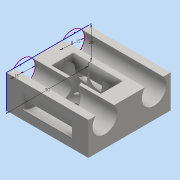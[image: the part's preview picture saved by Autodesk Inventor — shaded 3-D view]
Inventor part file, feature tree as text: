
AUTODESK INVENTOR PART (.ipt)
format: ipt  version: 2016 (Build 200138000, 138)  size: 208,384 bytes
history: native  units: mm
features: sketch x4, extrude x3, hole x1
ambient origin geometry x8: Origin, YZ Plane, XZ Plane, XY Plane, X Axis, Y Axis, Z Axis, Center Point
bodies: Body1 (feature_tree)
feature tree (8):
  sketch  "Sketch2"  dims[d22=50.0mm d23=20.0mm]
  extrude  "Extrusion2"  Depth=20.0mm
  extrude  "Extrusion3"  Depth=15.0mm
  extrude  "Extrusion4"  Depth=10.0mm
  hole  "Hole3"  [1 undecoded]
  sketch  "Sketch3"  dims[d24=15.0mm d25=15.0mm]
  sketch  "Sketch4"  dims[d26=10.0mm d27=0.0mm]
  sketch  "Sketch6"  dims[d28=50.0mm d29=20.0mm d30=15.0mm d31=15.0mm d32=30.0mm d33=0.0mm d34=50.0mm d35=20.0mm d36=15.0mm d37=15.0mm d38=10.0mm d39=0.0mm d47=3.0mm d48=25.0mm d49=3.0mm d50=4.5mm d51=10.0mm d52=3.0mm d53=4.5mm d54=3.2mm d55=6.0mm d56=8.0mm d57=15.0mm d58=90.0deg d59=8.0mm d60=20.594885mm d40=1.0mm d41=1.0mm]
note: 1 required parameter value undecoded (feature->parameter linkage not recoverable at this tier; creation-order binding heuristic only, values carry confidence <= 0.55)
